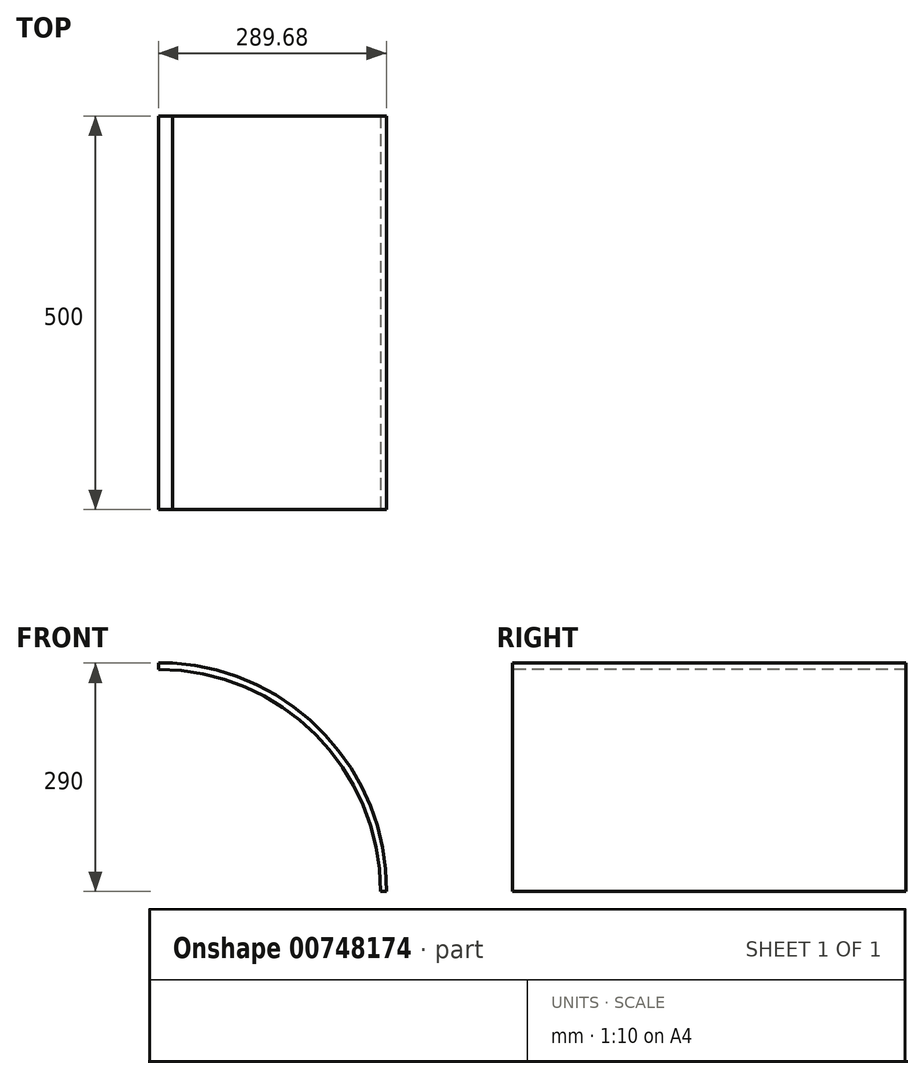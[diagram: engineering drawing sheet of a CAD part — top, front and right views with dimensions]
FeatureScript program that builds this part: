
annotation { "Feature Type Name" : "Feature", "Feature Type Description" : "" }
export const myFeature = defineFeature(function(context is Context, id is Id, definition is map)
    precondition{}
    {
        {
            var Q0;
            Q0=qCreatedBy(makeId("Front.planeOp"),FACE);
            var sketch = newSketch(context, id + "F0", { "sketchPlane" : qUnion([Q0])});
            skLineSegment(sketch, "E0", {"start": v(0, 0) * mm, "end": v(290, 0) * mm});
            skLineSegment(sketch, "E1", {"start": v(290, 0) * mm, "end": v(290, 290) * mm});
            skLineSegment(sketch, "E2", {"start": v(290, 290) * mm, "end": v(0, 290) * mm});
            skLineSegment(sketch, "E3", {"start": v(0, 290) * mm, "end": v(0, 0) * mm});
            skSolve(sketch);
        }
        {
            var Q0;
            Q0=qSketchRegion(id+"F0",true);
            extrude(context, id + "F1", {"entities" : qUnion([Q0]), "depth" : 500 * mm, "offsetDistance" : 25 * mm});
        }
        {
            var Q0;
            Q0=makeQuery(id+"F0.imprint","IMPRINT",FACE,{"disambiguationData":[TD([[makeQuery(id+"F0.imprint","IMPRINT",EDGE,{"derivedFrom":sQuery(id+"F0.wireOp",EDGE,"E0")}),1.0]])]});
            var sketch = newSketch(context, id + "F2", { "sketchPlane" : qUnion([Q0])});
            skArc(sketch, "E4", {"start": v(289.68, 0) * mm, "mid": v(205.4, 205.65) * mm, "end": v(0, 290.52) * mm});
            skSolve(sketch);
        }
        {
            var Q0;
            {var subQ5=makeQuery(id+"F0.imprint","IMPRINT",EDGE,{"derivedFrom":sQuery(id+"F0.wireOp",EDGE,"E1")});Q0=makeQuery(id+"F2.imprint","IMPRINT",FACE,{"disambiguationData":[TD([[makeQuery(id+"F2.imprint","IMPRINT",EDGE,{"derivedFrom":subQ5}),1.0]])]});}
            extrude(context, id + "F3", {"entities" : qUnion([Q0]), "operationType" : NewBodyOperationType.REMOVE, "depth" : 795 * mm, "offsetDistance" : 25 * mm});
        }
        {
            var Q0;
            Q0=makeQuery(id+"F1.opExtrude","CAP_FACE",FACE,{"disambiguationData":[OSD([sQuery(id+"F0.wireOp",EDGE,"E0"),sQuery(id+"F0.wireOp",EDGE,"E1"),sQuery(id+"F0.wireOp",EDGE,"E2"),sQuery(id+"F0.wireOp",EDGE,"E3")])],"isStart":false});
            var sketch = newSketch(context, id + "F4", { "sketchPlane" : qUnion([Q0])});
            skArc(sketch, "E5", {"start": v(282.12, 0) * mm, "mid": v(199.48, 199.53) * mm, "end": v(0, 282.28) * mm});
            skSolve(sketch);
        }
        {
            var Q0;
            {var subQ0=sQuery(id+"F4.wireOp",EDGE,"E5");Q0=makeQuery(id+"F4.imprint","IMPRINT",FACE,{"disambiguationData":[TD([[makeQuery(id+"F4.imprint","IMPRINT",EDGE,{"derivedFrom":subQ0}),1.0]])]});}
            extrude(context, id + "F5", {"entities" : qUnion([Q0]), "operationType" : NewBodyOperationType.REMOVE, "oppositeDirection" : true, "depth" : 770 * mm, "offsetDistance" : 25 * mm});
        }
    });
